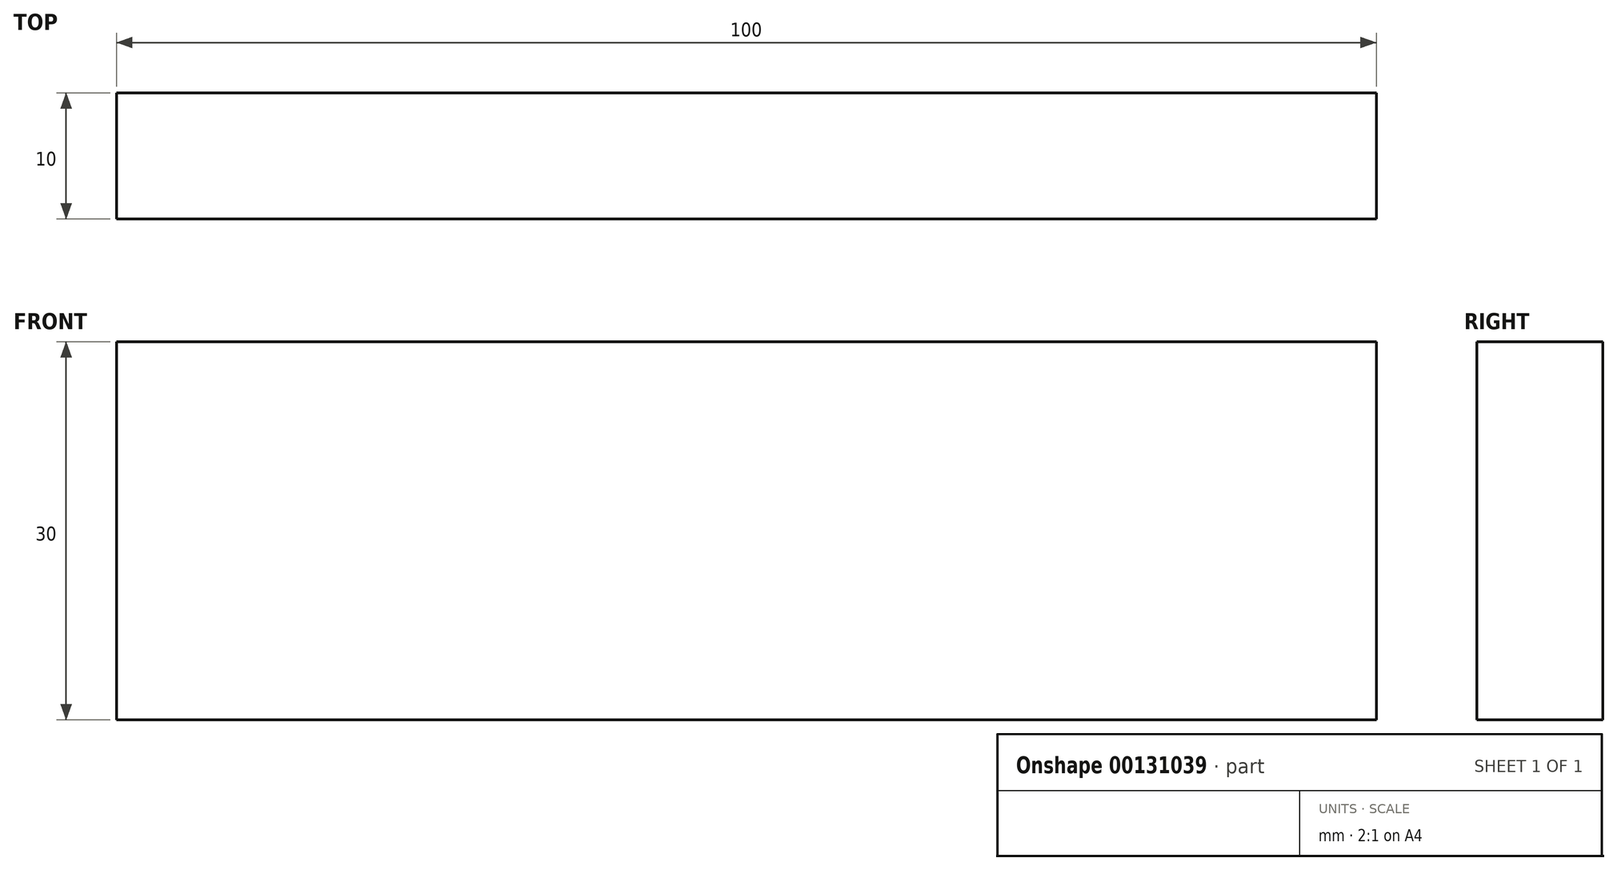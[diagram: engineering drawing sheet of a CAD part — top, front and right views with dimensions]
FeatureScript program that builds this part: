
annotation { "Feature Type Name" : "Feature", "Feature Type Description" : "" }
export const myFeature = defineFeature(function(context is Context, id is Id, definition is map)
    precondition{}
    {
        {
            var Q0;
            Q0=qCreatedBy(makeId("Front.planeOp"),FACE);
            var sketch = newSketch(context, id + "F0", { "sketchPlane" : qUnion([Q0])});
            skLineSegment(sketch, "E0.bottom", {"start": v(50, 15) * mm, "end": v(-50, 15) * mm});
            skLineSegment(sketch, "E0.top", {"start": v(50, -15) * mm, "end": v(-50, -15) * mm});
            skLineSegment(sketch, "E0.left", {"start": v(50, 15) * mm, "end": v(50, -15) * mm});
            skLineSegment(sketch, "E0.right", {"start": v(-50, 15) * mm, "end": v(-50, -15) * mm});
            skPoint(sketch, "E0.middle", {"position": v(0, 0) * mm});
            skSolve(sketch);
        }
        {
            var Q0;
            Q0=makeQuery(id+"F0.imprint","IMPRINT",FACE,{"disambiguationData":[TD([[makeQuery(id+"F0.imprint","IMPRINT",EDGE,{"derivedFrom":sQuery(id+"F0.wireOp",EDGE,"E0.bottom")}),1.0]])]});
            extrude(context, id + "F1", {"entities" : qUnion([Q0]), "depth" : 10 * mm});
        }
    });
